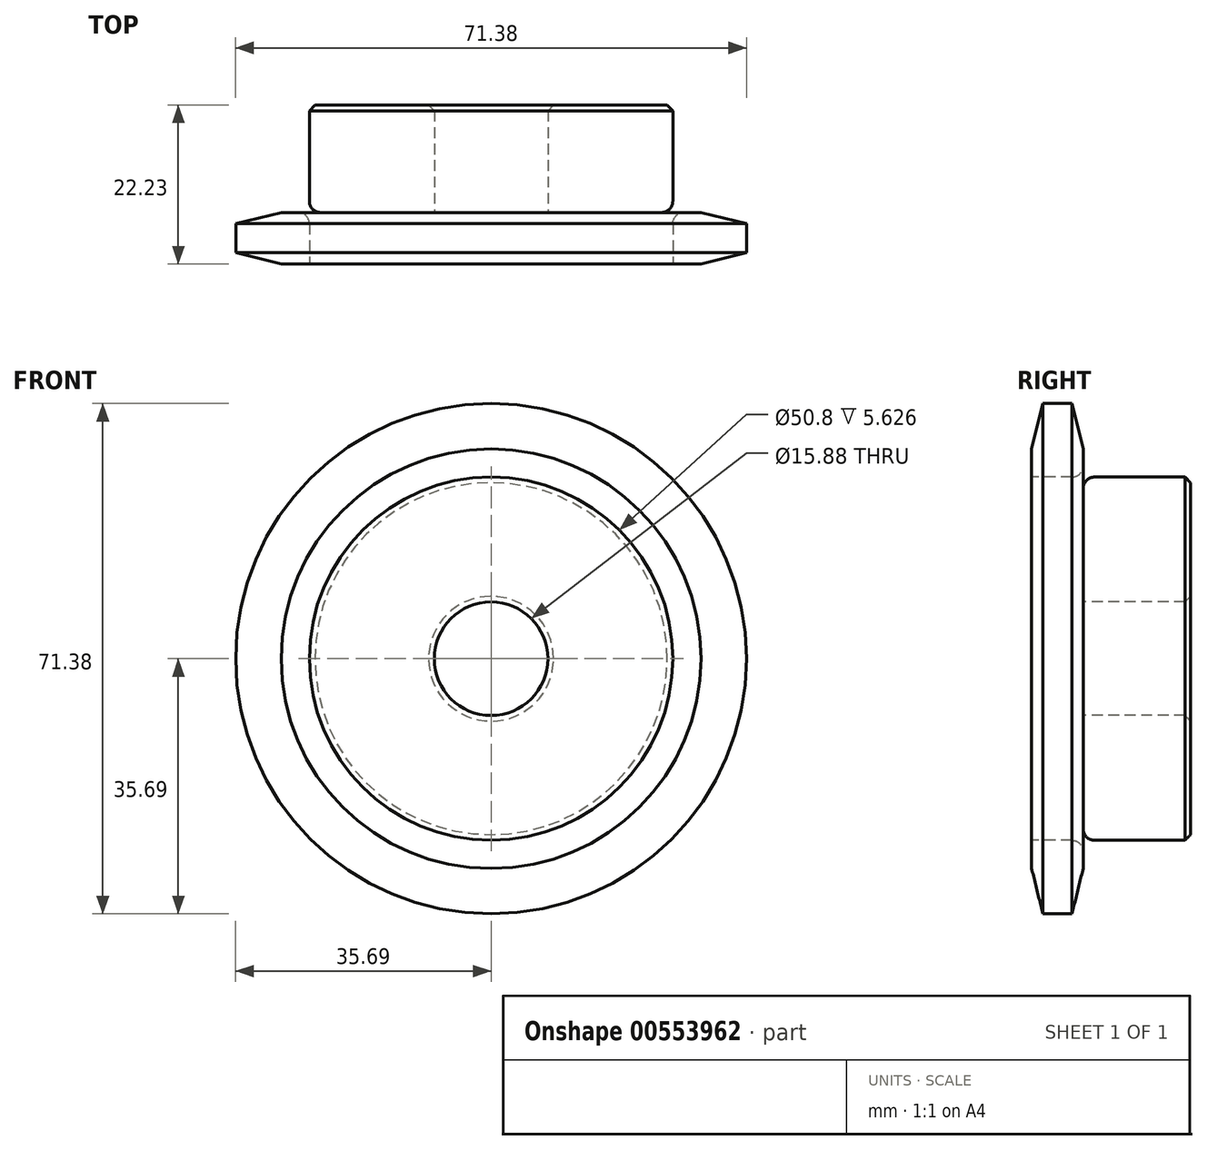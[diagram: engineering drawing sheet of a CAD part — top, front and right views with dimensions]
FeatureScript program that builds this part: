
annotation { "Feature Type Name" : "Feature", "Feature Type Description" : "" }
export const myFeature = defineFeature(function(context is Context, id is Id, definition is map)
    precondition{}
    {
        {
            var Q0;
            Q0=qCreatedBy(makeId("Right.planeOp"),FACE);
            var sketch = newSketch(context, id + "F0", { "sketchPlane" : qUnion([Q0])});
            skLineSegment(sketch, "E0", {"start": v(0, 0) * mm, "end": v(18.9, 0) * mm, "construction": true});
            skLineSegment(sketch, "E1.bottom", {"start": v(0, 7.94) * mm, "end": v(7.21, 7.94) * mm});
            skLineSegment(sketch, "E1.top", {"start": v(0, 35.69) * mm, "end": v(7.21, 35.69) * mm});
            skLineSegment(sketch, "E1.left", {"start": v(0, 7.94) * mm, "end": v(0, 35.69) * mm});
            skLineSegment(sketch, "E1.right", {"start": v(7.21, 7.94) * mm, "end": v(7.21, 35.69) * mm});
            skLineSegment(sketch, "E2.bottom", {"start": v(0, 7.94) * mm, "end": v(22.23, 7.94) * mm});
            skLineSegment(sketch, "E2.top", {"start": v(0, 25.4) * mm, "end": v(22.23, 25.4) * mm});
            skLineSegment(sketch, "E2.left", {"start": v(0, 7.94) * mm, "end": v(0, 25.4) * mm});
            skLineSegment(sketch, "E2.right", {"start": v(22.23, 7.94) * mm, "end": v(22.22, 25.4) * mm});
            skLineSegment(sketch, "E3.MirrorCS", {"start": v(0, -7.94) * mm, "end": v(7.21, -7.94) * mm});
            skLineSegment(sketch, "E4.MirrorCS", {"start": v(0, -35.69) * mm, "end": v(7.21, -35.69) * mm});
            skLineSegment(sketch, "E5.MirrorCS", {"start": v(0, -7.94) * mm, "end": v(0, -35.69) * mm});
            skLineSegment(sketch, "E6.MirrorCS", {"start": v(0, -25.4) * mm, "end": v(22.23, -25.4) * mm});
            skLineSegment(sketch, "E7.MirrorCS", {"start": v(7.21, -7.94) * mm, "end": v(7.21, -35.69) * mm});
            skLineSegment(sketch, "E8.MirrorCS", {"start": v(0, -7.94) * mm, "end": v(22.23, -7.94) * mm});
            skLineSegment(sketch, "E9.MirrorCS", {"start": v(22.23, -7.94) * mm, "end": v(22.23, -25.4) * mm});
            skLineSegment(sketch, "E10.MirrorCS", {"start": v(0, -7.94) * mm, "end": v(0, -25.4) * mm});
            skSolve(sketch);
        }
        {
            var Q0;
            {var subQ5=sQuery(id+"F0.wireOp",EDGE,"E2.right");Q0=makeQuery(id+"F0.imprint","IMPRINT",FACE,{"disambiguationData":[TD([[makeQuery(id+"F0.imprint","IMPRINT",EDGE,{"derivedFrom":subQ5}),1.0]])]});}
            var Q1;
            {var subQ5=sQuery(id+"F0.wireOp",EDGE,"E2.left");Q1=makeQuery(id+"F0.imprint","IMPRINT",FACE,{"disambiguationData":[TD([[makeQuery(id+"F0.imprint","IMPRINT",EDGE,{"derivedFrom":subQ5}),-1.0]])]});}
            var Q2;
            {var subQ0=sQuery(id+"F0.wireOp",EDGE,"E1.top");Q2=makeQuery(id+"F0.imprint","IMPRINT",FACE,{"disambiguationData":[TD([[makeQuery(id+"F0.imprint","IMPRINT",EDGE,{"derivedFrom":subQ0}),-1.0]])]});}
            var Q3;
            Q3=sQuery(id+"F0.wireOp",EDGE,"E0");
            revolve(context, id + "F1", {"entities" : qUnion([Q0, Q1, Q2]), "axis" : qUnion([Q3]), "revolveType" : RevolveType.FULL});
        }
        {
            var Q0;
            Q0=makeQuery(id+"F1.opRevolve","SWEPT_EDGE",EDGE,{"disambiguationData":[OSD([sQuery(id+"F0.wireOp",EDGE,"E1.right"),sQuery(id+"F0.wireOp",EDGE,"E2.top")])]});
            fillet(context, id + "F2", {"entities" : qUnion([Q0]), "radius" : 1.59 * mm, "tangentPropagation" : true, "allowEdgeOverflow" : false});
        }
        {
            var Q0;
            Q0=makeQuery(id+"F1.opRevolve","SWEPT_FACE",FACE,{"disambiguationData":[OSD([sQuery(id+"F0.wireOp",EDGE,"E2.right")])]});
            chamfer(context, id + "F3", {"entities" : qUnion([Q0]), "width" : 0.8 * mm, "tangentPropagation" : true});
        }
        {
            var Q0;
            Q0=makeQuery(id+"F1.opRevolve","SWEPT_EDGE",EDGE,{"disambiguationData":[OSD([sQuery(id+"F0.wireOp",EDGE,"E1.top"),sQuery(id+"F0.wireOp",EDGE,"E1.left")])]});
            var Q1;
            Q1=makeQuery(id+"F1.opRevolve","SWEPT_EDGE",EDGE,{"disambiguationData":[OSD([sQuery(id+"F0.wireOp",EDGE,"E1.top"),sQuery(id+"F0.wireOp",EDGE,"E1.right")])]});
            chamfer(context, id + "F4", {"entities" : qUnion([Q0, Q1]), "chamferType" : ChamferType.TWO_OFFSETS, "width1" : 6.35 * mm, "oppositeDirection" : false, "width2" : 1.57 * mm, "tangentPropagation" : true});
        }
    });
